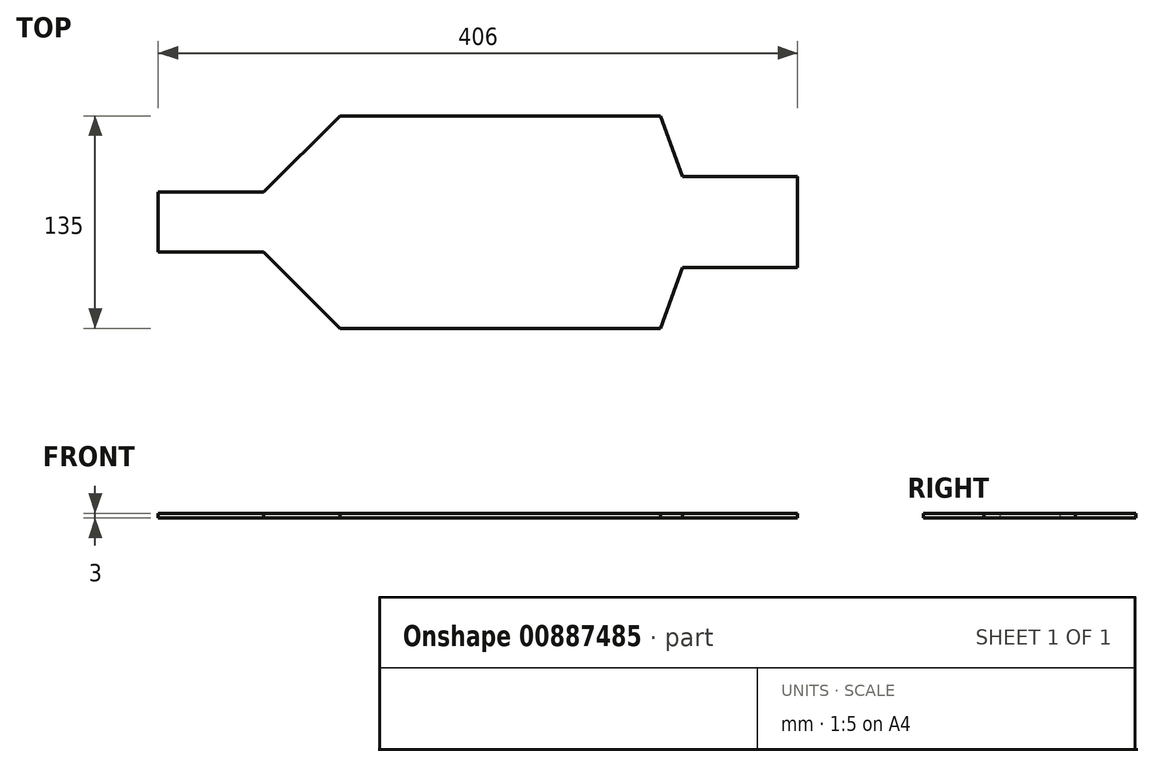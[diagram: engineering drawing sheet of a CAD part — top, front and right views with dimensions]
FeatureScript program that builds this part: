
annotation { "Feature Type Name" : "Feature", "Feature Type Description" : "" }
export const myFeature = defineFeature(function(context is Context, id is Id, definition is map)
    precondition{}
    {
        {
            var Q0;
            Q0=qCreatedBy(makeId("Top.planeOp"),FACE);
            var sketch = newSketch(context, id + "F0", { "sketchPlane" : qUnion([Q0])});
            skLineSegment(sketch, "E0.bottom", {"start": v(203, -67.5) * mm, "end": v(-203, -67.5) * mm, "construction": true});
            skLineSegment(sketch, "E0.top", {"start": v(203, 67.5) * mm, "end": v(-203, 67.5) * mm, "construction": true});
            skLineSegment(sketch, "E0.left", {"start": v(203, -67.5) * mm, "end": v(203, 67.5) * mm, "construction": true});
            skLineSegment(sketch, "E0.right", {"start": v(-203, -67.5) * mm, "end": v(-203, 67.5) * mm, "construction": true});
            skPoint(sketch, "E0.middle", {"position": v(0, 0) * mm});
            skPoint(sketch, "E1", {"position": v(-87.5, -67.5) * mm});
            skLineSegment(sketch, "E2", {"start": v(-87.5, -67.5) * mm, "end": v(-87.5, 67.5) * mm});
            skLineSegment(sketch, "E3", {"start": v(115.99, -67.5) * mm, "end": v(115.99, 67.5) * mm});
            skLineSegment(sketch, "E4", {"start": v(-136, 67.5) * mm, "end": v(-136, -67.5) * mm, "construction": true});
            skPoint(sketch, "E5", {"position": v(-136, -19) * mm});
            skPoint(sketch, "E6", {"position": v(-136, 19) * mm});
            skLineSegment(sketch, "E7", {"start": v(-136, 19) * mm, "end": v(-136, -19) * mm});
            skPoint(sketch, "E8", {"position": v(-136, 0) * mm});
            skLineSegment(sketch, "E9", {"start": v(-87.5, -67.5) * mm, "end": v(-136, -19) * mm});
            skLineSegment(sketch, "E10", {"start": v(-136, 19) * mm, "end": v(-87.5, 67.5) * mm});
            skLineSegment(sketch, "E11", {"start": v(-136, -19) * mm, "end": v(-203, -19) * mm});
            skLineSegment(sketch, "E12", {"start": v(-136, 19) * mm, "end": v(-203, 19) * mm});
            skLineSegment(sketch, "E13", {"start": v(-203, -19) * mm, "end": v(-203, 19) * mm});
            skLineSegment(sketch, "E14", {"start": v(-87.5, -67.5) * mm, "end": v(115.99, -67.5) * mm});
            skLineSegment(sketch, "E15", {"start": v(-87.5, 67.5) * mm, "end": v(115.99, 67.5) * mm});
            skLineSegment(sketch, "E16", {"start": v(130, -67.5) * mm, "end": v(130, 67.5) * mm});
            skPoint(sketch, "E17", {"position": v(130, -29) * mm});
            skPoint(sketch, "E18", {"position": v(130, 29) * mm});
            skLineSegment(sketch, "E19", {"start": v(130, -29) * mm, "end": v(130, 29) * mm});
            skPoint(sketch, "E20", {"position": v(130, 0) * mm});
            skLineSegment(sketch, "E21", {"start": v(115.99, -67.5) * mm, "end": v(130, -29) * mm});
            skLineSegment(sketch, "E22", {"start": v(115.99, 67.5) * mm, "end": v(130, 29) * mm});
            skLineSegment(sketch, "E23", {"start": v(130, 29) * mm, "end": v(203, 29) * mm});
            skLineSegment(sketch, "E24", {"start": v(130, -29) * mm, "end": v(203, -29) * mm});
            skLineSegment(sketch, "E25", {"start": v(203, 29) * mm, "end": v(203, -29) * mm});
            skSolve(sketch);
        }
        {
            var Q0;
            Q0 = qSketchRegion(id + "F0", true);
            extrude(context, id + "F1", {"entities" : qUnion([Q0]), "depth" : 3 * mm, "offsetDistance" : 25 * mm});
        }
    });
